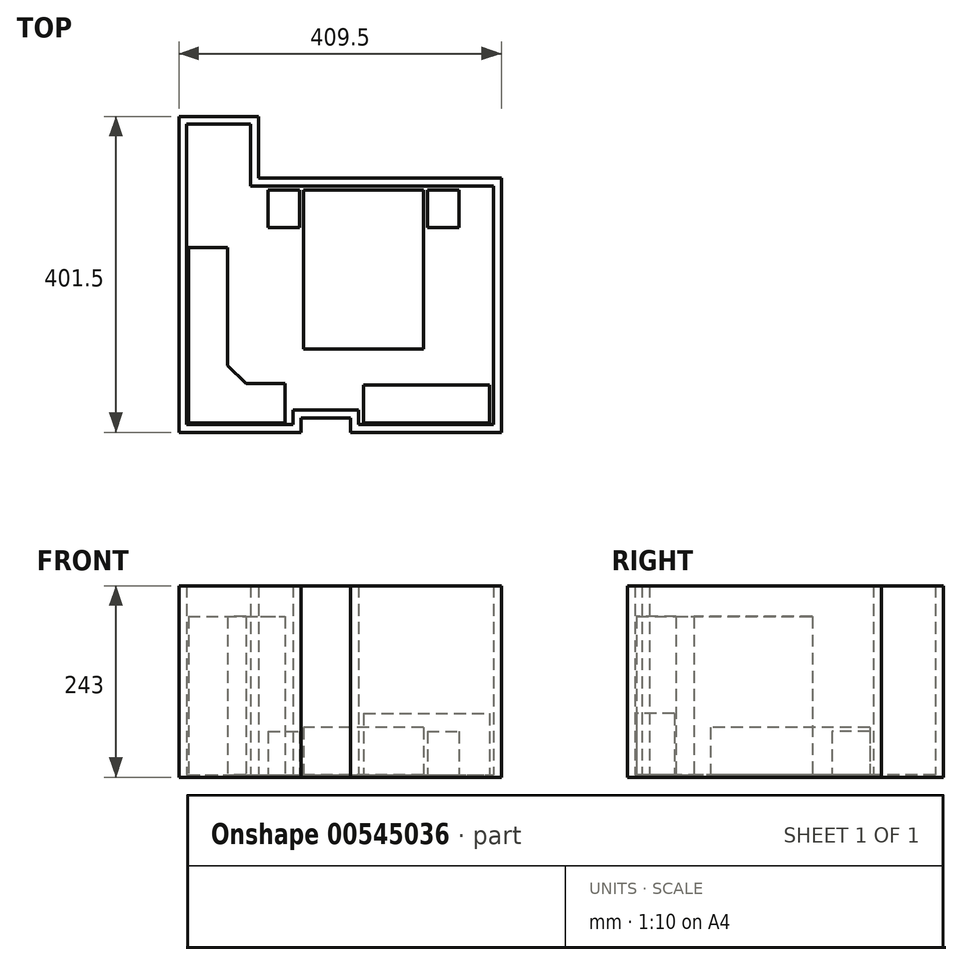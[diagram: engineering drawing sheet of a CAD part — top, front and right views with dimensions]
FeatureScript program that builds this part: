
annotation { "Feature Type Name" : "Feature", "Feature Type Description" : "" }
export const myFeature = defineFeature(function(context is Context, id is Id, definition is map)
    precondition{}
    {
        {
            var Q0;
            Q0=qCreatedBy(makeId("Top.planeOp"),FACE);
            var sketch = newSketch(context, id + "F0", { "sketchPlane" : qUnion([Q0])});
            skLineSegment(sketch, "E0", {"start": v(0, 0) * mm, "end": v(0, 0) * mm});
            skLineSegment(sketch, "E1", {"start": v(0, 0) * mm, "end": v(0, -381.5) * mm});
            skLineSegment(sketch, "E2", {"start": v(0, -381.5) * mm, "end": v(135, -381.5) * mm});
            skLineSegment(sketch, "E3", {"start": v(135, -381.5) * mm, "end": v(135, -363) * mm});
            skLineSegment(sketch, "E4", {"start": v(135, -363) * mm, "end": v(218, -363) * mm});
            skLineSegment(sketch, "E5", {"start": v(218, -363) * mm, "end": v(218, -381.5) * mm});
            skLineSegment(sketch, "E6", {"start": v(218, -381.5) * mm, "end": v(389.5, -381.5) * mm});
            skLineSegment(sketch, "E7", {"start": v(389.5, -381.5) * mm, "end": v(389.5, -78.5) * mm});
            skLineSegment(sketch, "E8", {"start": v(0, 0) * mm, "end": v(81, 0) * mm});
            skLineSegment(sketch, "E9", {"start": v(81, 0) * mm, "end": v(81, -78.5) * mm});
            skLineSegment(sketch, "E10", {"start": v(81, -78.5) * mm, "end": v(389.5, -78.5) * mm});
            skLineSegment(sketch, "E11.0", {"start": v(145, -373) * mm, "end": v(208, -373) * mm});
            skLineSegment(sketch, "E11.1", {"start": v(145, -391.5) * mm, "end": v(145, -373) * mm});
            skLineSegment(sketch, "E11.2", {"start": v(208, -373) * mm, "end": v(208, -391.5) * mm});
            skLineSegment(sketch, "E11.3", {"start": v(-10, -391.5) * mm, "end": v(145, -391.5) * mm});
            skLineSegment(sketch, "E11.4", {"start": v(-10, 10) * mm, "end": v(-10, -391.5) * mm});
            skLineSegment(sketch, "E11.5", {"start": v(-10, 10) * mm, "end": v(91, 10) * mm});
            skLineSegment(sketch, "E11.6", {"start": v(208, -391.5) * mm, "end": v(399.5, -391.5) * mm});
            skLineSegment(sketch, "E11.7", {"start": v(399.5, -391.5) * mm, "end": v(399.5, -68.5) * mm});
            skLineSegment(sketch, "E11.8", {"start": v(91, -68.5) * mm, "end": v(399.5, -68.5) * mm});
            skLineSegment(sketch, "E11.9", {"start": v(91, 10) * mm, "end": v(91, -68.5) * mm});
            skLineSegment(sketch, "E12.bottom", {"start": v(300.5, -83.5) * mm, "end": v(148.5, -83.5) * mm});
            skLineSegment(sketch, "E12.top", {"start": v(300.5, -285.5) * mm, "end": v(148.5, -285.5) * mm});
            skLineSegment(sketch, "E12.left", {"start": v(300.5, -83.5) * mm, "end": v(300.5, -285.5) * mm});
            skLineSegment(sketch, "E12.right", {"start": v(148.5, -83.5) * mm, "end": v(148.5, -285.5) * mm});
            skLineSegment(sketch, "E13.bottom", {"start": v(103.5, -83.5) * mm, "end": v(143.5, -83.5) * mm});
            skLineSegment(sketch, "E13.top", {"start": v(103.5, -131.5) * mm, "end": v(143.5, -131.5) * mm});
            skLineSegment(sketch, "E13.left", {"start": v(103.5, -83.5) * mm, "end": v(103.5, -131.5) * mm});
            skLineSegment(sketch, "E13.right", {"start": v(143.5, -83.5) * mm, "end": v(143.5, -131.5) * mm});
            skLineSegment(sketch, "E14.bottom", {"start": v(305.5, -83.5) * mm, "end": v(345.5, -83.5) * mm});
            skLineSegment(sketch, "E14.top", {"start": v(305.5, -131.5) * mm, "end": v(345.5, -131.5) * mm});
            skLineSegment(sketch, "E14.left", {"start": v(305.5, -83.5) * mm, "end": v(305.5, -131.5) * mm});
            skLineSegment(sketch, "E14.right", {"start": v(345.5, -83.5) * mm, "end": v(345.5, -131.5) * mm});
            skLineSegment(sketch, "E15.bottom", {"start": v(224.5, -331.5) * mm, "end": v(384.5, -331.5) * mm});
            skLineSegment(sketch, "E15.top", {"start": v(224.5, -379.5) * mm, "end": v(384.5, -379.5) * mm});
            skLineSegment(sketch, "E15.left", {"start": v(224.5, -331.5) * mm, "end": v(224.5, -379.5) * mm});
            skLineSegment(sketch, "E15.right", {"start": v(384.5, -331.5) * mm, "end": v(384.5, -379.5) * mm});
            skLineSegment(sketch, "E16", {"start": v(2, -156.5) * mm, "end": v(52, -156.5) * mm});
            skLineSegment(sketch, "E17", {"start": v(52, -156.5) * mm, "end": v(52, -306.5) * mm});
            skLineSegment(sketch, "E18", {"start": v(52, -306.5) * mm, "end": v(2, -306.5) * mm});
            skLineSegment(sketch, "E19", {"start": v(2, -306.5) * mm, "end": v(2, -156.5) * mm});
            skLineSegment(sketch, "E20", {"start": v(2, -306.5) * mm, "end": v(2, -379.5) * mm});
            skLineSegment(sketch, "E21", {"start": v(2, -379.5) * mm, "end": v(75, -379.5) * mm});
            skLineSegment(sketch, "E22", {"start": v(75, -379.5) * mm, "end": v(75, -329.5) * mm});
            skLineSegment(sketch, "E23", {"start": v(75, -329.5) * mm, "end": v(52, -306.5) * mm});
            skLineSegment(sketch, "E24", {"start": v(75, -329.5) * mm, "end": v(125, -329.5) * mm});
            skLineSegment(sketch, "E25", {"start": v(125, -329.5) * mm, "end": v(125, -379.5) * mm});
            skLineSegment(sketch, "E26", {"start": v(125, -379.5) * mm, "end": v(75, -379.5) * mm});
            skSolve(sketch);
        }
        {
            var Q0;
            Q0 = qSketchRegion(id + "F0", true);
            extrude(context, id + "F1", {"entities" : qUnion([Q0]), "depth" : 240 * mm, "offsetDistance" : 25 * mm});
        }
        {
            var Q0;
            Q0 = qSketchRegion(id + "F0", true);
            var Q1;
            Q1=makeQuery(id+"F0.imprint","IMPRINT",FACE,{"disambiguationData":[TD([[makeQuery(id+"F0.imprint","IMPRINT",EDGE,{"derivedFrom":sQuery(id+"F0.wireOp",EDGE,"E1")}),1.0]])]});
            var Q2;
            Q2=makeQuery(id+"F0.imprint","IMPRINT",FACE,{"disambiguationData":[TD([[makeQuery(id+"F0.imprint","IMPRINT",EDGE,{"derivedFrom":sQuery(id+"F0.wireOp",EDGE,"E16")}),-1.0]])]});
            var Q3;
            Q3=makeQuery(id+"F0.imprint","IMPRINT",FACE,{"disambiguationData":[TD([[makeQuery(id+"F0.imprint","IMPRINT",EDGE,{"derivedFrom":sQuery(id+"F0.wireOp",EDGE,"E12.bottom")}),1.0]])]});
            var Q4;
            Q4=makeQuery(id+"F0.imprint","IMPRINT",FACE,{"disambiguationData":[TD([[makeQuery(id+"F0.imprint","IMPRINT",EDGE,{"derivedFrom":sQuery(id+"F0.wireOp",EDGE,"E13.bottom")}),-1.0]])]});
            var Q5;
            Q5=makeQuery(id+"F0.imprint","IMPRINT",FACE,{"disambiguationData":[TD([[makeQuery(id+"F0.imprint","IMPRINT",EDGE,{"derivedFrom":sQuery(id+"F0.wireOp",EDGE,"E14.bottom")}),-1.0]])]});
            var Q6;
            Q6=makeQuery(id+"F0.imprint","IMPRINT",FACE,{"disambiguationData":[TD([[makeQuery(id+"F0.imprint","IMPRINT",EDGE,{"derivedFrom":sQuery(id+"F0.wireOp",EDGE,"E15.bottom")}),-1.0]])]});
            var Q7;
            Q7=makeQuery(id+"F0.imprint","IMPRINT",FACE,{"disambiguationData":[TD([[makeQuery(id+"F0.imprint","IMPRINT",EDGE,{"derivedFrom":sQuery(id+"F0.wireOp",EDGE,"E18")}),1.0]])]});
            var Q8;
            Q8=makeQuery(id+"F0.imprint","IMPRINT",FACE,{"disambiguationData":[TD([[makeQuery(id+"F0.imprint","IMPRINT",EDGE,{"derivedFrom":sQuery(id+"F0.wireOp",EDGE,"E22")}),-1.0]])]});
            extrude(context, id + "F2", {"entities" : qUnion([Q0, Q1, Q2, Q3, Q4, Q5, Q6, Q7, Q8]), "operationType" : NewBodyOperationType.ADD, "oppositeDirection" : true, "depth" : 3 * mm, "offsetDistance" : 25 * mm});
        }
        {
            var Q0;
            Q0=makeQuery(id+"F0.imprint","IMPRINT",FACE,{"disambiguationData":[TD([[makeQuery(id+"F0.imprint","IMPRINT",EDGE,{"derivedFrom":sQuery(id+"F0.wireOp",EDGE,"E16")}),-1.0]])]});
            var Q1;
            Q1=makeQuery(id+"F0.imprint","IMPRINT",FACE,{"disambiguationData":[TD([[makeQuery(id+"F0.imprint","IMPRINT",EDGE,{"derivedFrom":sQuery(id+"F0.wireOp",EDGE,"E18")}),1.0]])]});
            var Q2;
            Q2=makeQuery(id+"F0.imprint","IMPRINT",FACE,{"disambiguationData":[TD([[makeQuery(id+"F0.imprint","IMPRINT",EDGE,{"derivedFrom":sQuery(id+"F0.wireOp",EDGE,"E22")}),-1.0]])]});
            extrude(context, id + "F3", {"entities" : qUnion([Q0, Q1, Q2]), "depth" : 201 * mm, "offsetDistance" : 25 * mm});
        }
        {
            var Q0;
            Q0=makeQuery(id+"F0.imprint","IMPRINT",FACE,{"disambiguationData":[TD([[makeQuery(id+"F0.imprint","IMPRINT",EDGE,{"derivedFrom":sQuery(id+"F0.wireOp",EDGE,"E13.bottom")}),-1.0]])]});
            var Q1;
            Q1=makeQuery(id+"F0.imprint","IMPRINT",FACE,{"disambiguationData":[TD([[makeQuery(id+"F0.imprint","IMPRINT",EDGE,{"derivedFrom":sQuery(id+"F0.wireOp",EDGE,"E14.bottom")}),-1.0]])]});
            extrude(context, id + "F4", {"entities" : qUnion([Q0, Q1]), "depth" : 55 * mm, "offsetDistance" : 25 * mm});
        }
        {
            var Q0;
            Q0=makeQuery(id+"F0.imprint","IMPRINT",FACE,{"disambiguationData":[TD([[makeQuery(id+"F0.imprint","IMPRINT",EDGE,{"derivedFrom":sQuery(id+"F0.wireOp",EDGE,"E12.bottom")}),1.0]])]});
            extrude(context, id + "F5", {"entities" : qUnion([Q0]), "depth" : 60 * mm, "offsetDistance" : 25 * mm});
        }
        {
            var Q0;
            Q0=makeQuery(id+"F0.imprint","IMPRINT",FACE,{"disambiguationData":[TD([[makeQuery(id+"F0.imprint","IMPRINT",EDGE,{"derivedFrom":sQuery(id+"F0.wireOp",EDGE,"E15.bottom")}),-1.0]])]});
            extrude(context, id + "F6", {"entities" : qUnion([Q0]), "depth" : 78 * mm, "offsetDistance" : 25 * mm});
        }
    });
